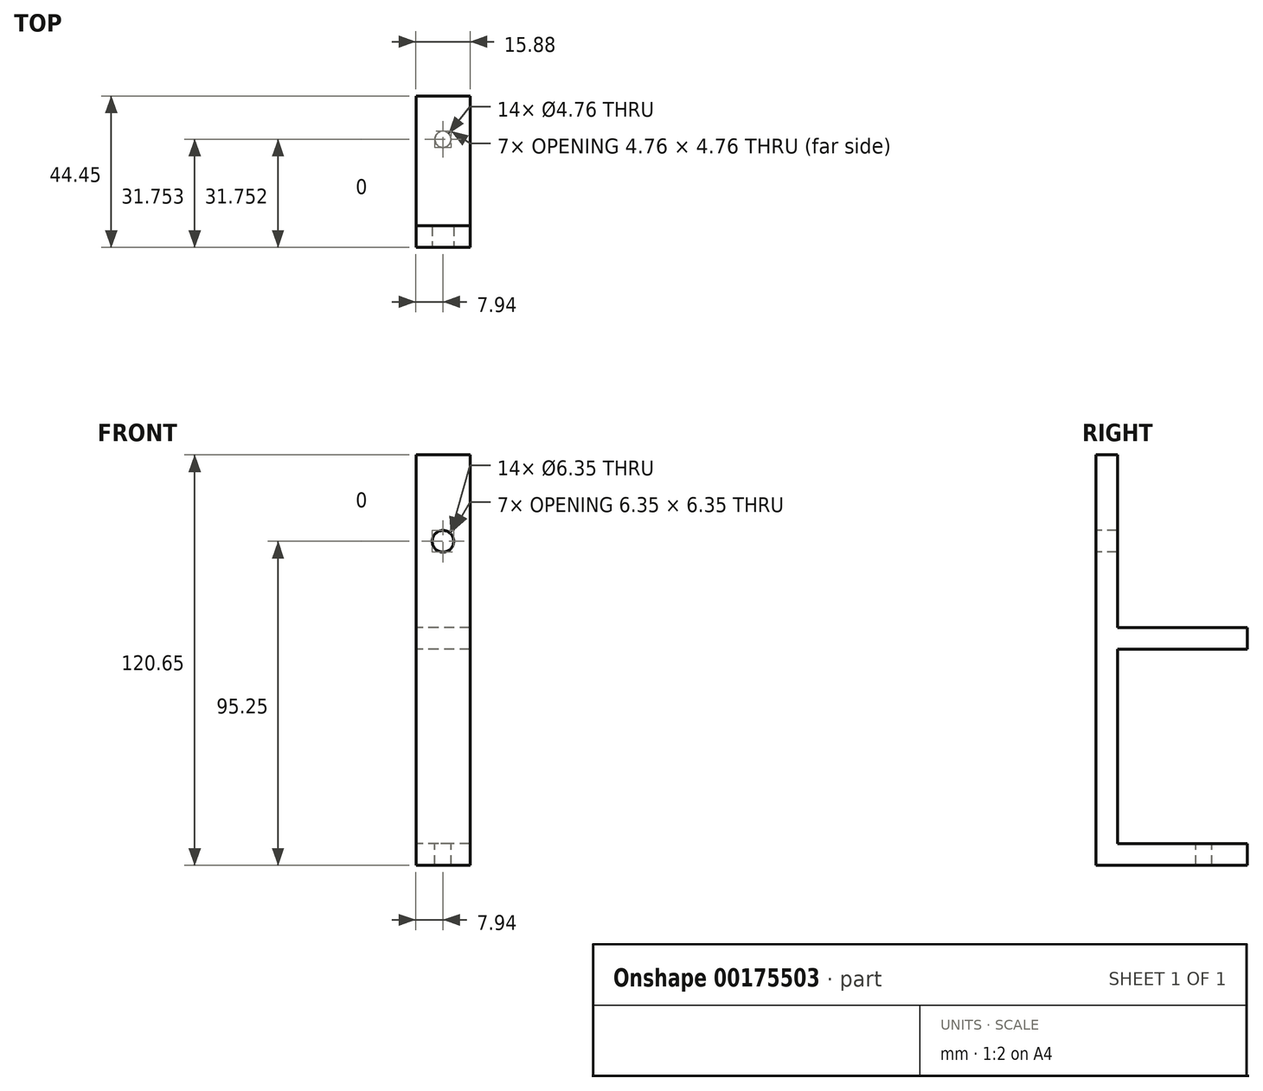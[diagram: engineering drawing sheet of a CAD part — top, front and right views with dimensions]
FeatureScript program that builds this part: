
annotation { "Feature Type Name" : "Feature", "Feature Type Description" : "" }
export const myFeature = defineFeature(function(context is Context, id is Id, definition is map)
    precondition{}
    {
        {
            var Q0;
            Q0=qCreatedBy(makeId("Right.planeOp"),FACE);
            var sketch = newSketch(context, id + "F0", { "sketchPlane" : qUnion([Q0])});
            skLineSegment(sketch, "E0.bottom", {"start": v(4.76, 50.8) * mm, "end": v(-1.59, 50.8) * mm});
            skLineSegment(sketch, "E0.left", {"start": v(4.76, 50.8) * mm, "end": v(4.76, 0) * mm});
            skLineSegment(sketch, "E0.right", {"start": v(-1.59, 50.8) * mm, "end": v(-1.59, 0) * mm});
            skPoint(sketch, "E0.middle", {"position": v(0, 0) * mm});
            skLineSegment(sketch, "E1", {"start": v(-1.59, 0) * mm, "end": v(-1.59, -69.85) * mm});
            skLineSegment(sketch, "E2", {"start": v(4.76, -6.35) * mm, "end": v(4.76, -63.5) * mm});
            skLineSegment(sketch, "E3", {"start": v(4.76, -69.85) * mm, "end": v(-1.59, -69.85) * mm});
            skLineSegment(sketch, "E4.bottom", {"start": v(4.76, 0) * mm, "end": v(42.86, 0) * mm});
            skLineSegment(sketch, "E4.top", {"start": v(4.76, -6.35) * mm, "end": v(42.86, -6.35) * mm});
            skLineSegment(sketch, "E4.right", {"start": v(42.86, 0) * mm, "end": v(42.86, -6.35) * mm});
            skLineSegment(sketch, "E5.bottom", {"start": v(4.76, -69.85) * mm, "end": v(42.86, -69.85) * mm});
            skLineSegment(sketch, "E5.top", {"start": v(4.76, -63.5) * mm, "end": v(42.86, -63.5) * mm});
            skLineSegment(sketch, "E5.right", {"start": v(42.86, -69.85) * mm, "end": v(42.86, -63.5) * mm});
            skSolve(sketch);
        }
        {
            var Q0;
            Q0 = qSketchRegion(id + "F0", true);
            extrude(context, id + "F1", {"entities" : qUnion([Q0]), "endBound" : BoundingType.SYMMETRIC, "depth" : 15.88 * mm});
        }
        {
            var Q0;
            Q0=makeQuery(id+"F1.opExtrude","SWEPT_FACE",FACE,{"disambiguationData":[OSD([sQuery(id+"F0.wireOp",EDGE,"E5.top")])]});
            var sketch = newSketch(context, id + "F2", { "sketchPlane" : qUnion([Q0])});
            skLineSegment(sketch, "E6", {"start": v(0, 4.76) * mm, "end": v(0, 30.16) * mm});
            skPoint(sketch, "E6.endSnap0", {"position": v(0, 4.76) * mm});
            skCircle(sketch, "E7", {"center": v(0, 30.16) * mm, "radius": 2.38 * mm});
            skSolve(sketch);
        }
        {
            var Q0;
            Q0=makeQuery(id+"F1.opExtrude","SWEPT_FACE",FACE,{"disambiguationData":[OSD([sQuery(id+"F0.wireOp",EDGE,"E0.right"),sQuery(id+"F0.wireOp",EDGE,"E1")])]});
            var sketch = newSketch(context, id + "F3", { "sketchPlane" : qUnion([Q0])});
            skLineSegment(sketch, "E8", {"start": v(0, 0) * mm, "end": v(0, 25.4) * mm});
            skCircle(sketch, "E9", {"center": v(0, 25.4) * mm, "radius": 3.18 * mm});
            skSolve(sketch);
        }
        {
            var Q0;
            Q0 = qSketchRegion(id + "F3", true);
            extrude(context, id + "F4", {"entities" : qUnion([Q0]), "operationType" : NewBodyOperationType.REMOVE, "oppositeDirection" : true, "depth" : 25.4 * mm});
        }
        {
            var Q0;
            Q0=makeQuery(id+"F2.imprint","IMPRINT",FACE,{"disambiguationData":[TD([[makeQuery(id+"F2.imprint","IMPRINT",EDGE,{"derivedFrom":sQuery(id+"F2.wireOp",EDGE,"E7")}),1.0]])]});
            extrude(context, id + "F5", {"entities" : qUnion([Q0]), "operationType" : NewBodyOperationType.REMOVE, "oppositeDirection" : true, "depth" : 25.4 * mm});
        }
    });
